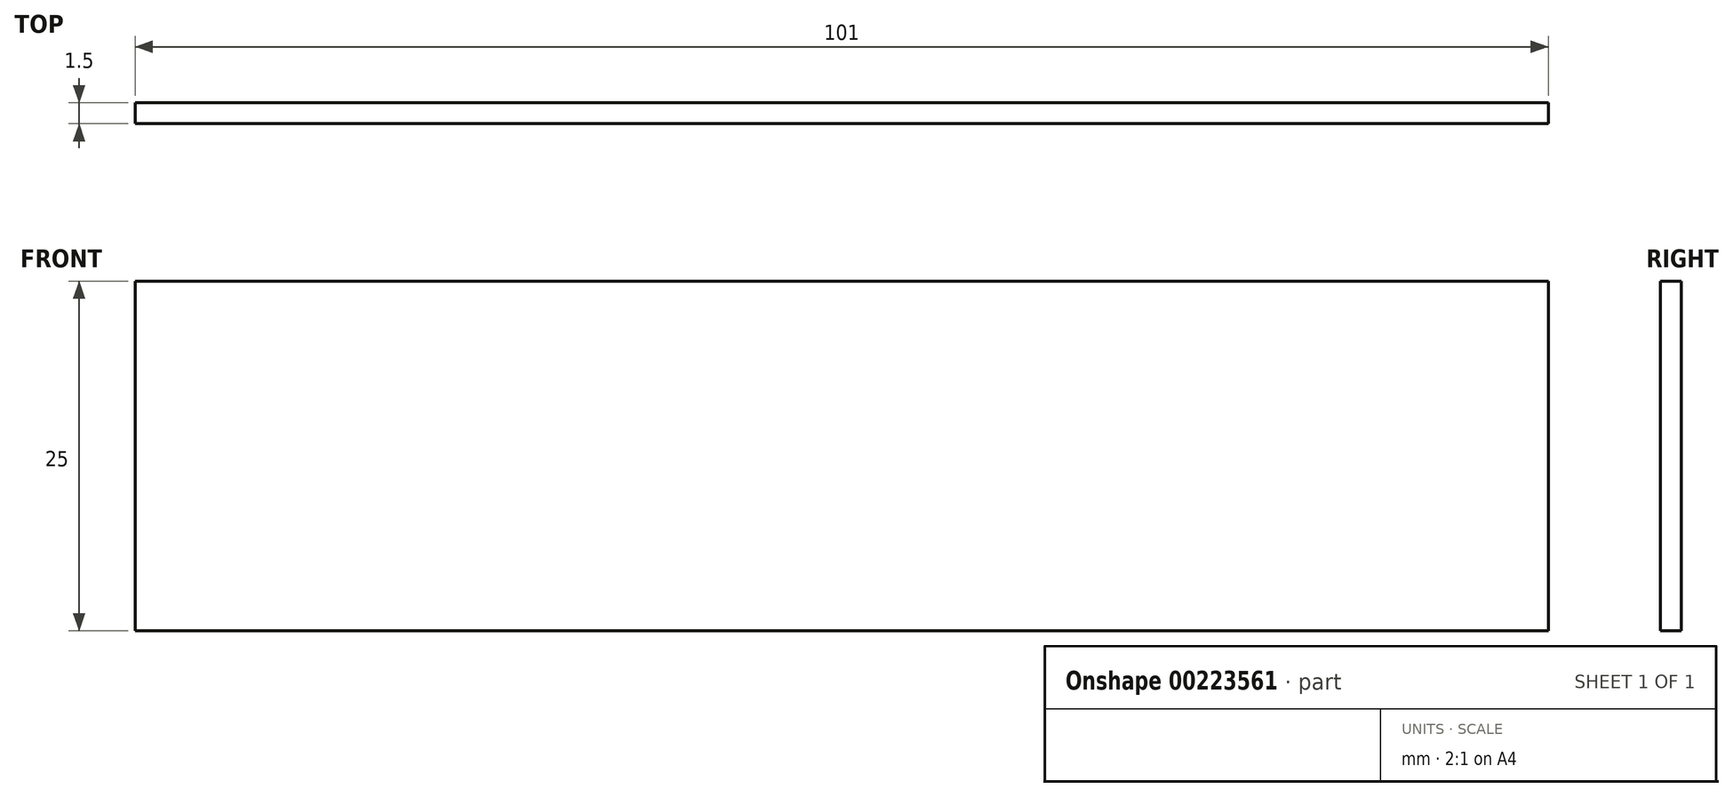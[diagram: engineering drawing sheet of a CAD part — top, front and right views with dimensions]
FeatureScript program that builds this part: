
annotation { "Feature Type Name" : "Feature", "Feature Type Description" : "" }
export const myFeature = defineFeature(function(context is Context, id is Id, definition is map)
    precondition{}
    {
        {
            var Q0;
            Q0=qCreatedBy(makeId("Front.planeOp"),FACE);
            var sketch = newSketch(context, id + "F0", { "sketchPlane" : qUnion([Q0])});
            skLineSegment(sketch, "E0.bottom", {"start": v(50.5, -12.5) * mm, "end": v(-50.5, -12.5) * mm});
            skLineSegment(sketch, "E0.top", {"start": v(50.5, 12.5) * mm, "end": v(-50.5, 12.5) * mm});
            skLineSegment(sketch, "E0.left", {"start": v(50.5, -12.5) * mm, "end": v(50.5, 12.5) * mm});
            skLineSegment(sketch, "E0.right", {"start": v(-50.5, -12.5) * mm, "end": v(-50.5, 12.5) * mm});
            skPoint(sketch, "E0.middle", {"position": v(0, 0) * mm});
            skSolve(sketch);
        }
        {
            var Q0;
            Q0=makeQuery(id+"F0.imprint","IMPRINT",FACE,{"disambiguationData":[TD([[makeQuery(id+"F0.imprint","IMPRINT",EDGE,{"derivedFrom":sQuery(id+"F0.wireOp",EDGE,"E0.bottom")}),-1.0]])]});
            extrude(context, id + "F1", {"entities" : qUnion([Q0]), "depth" : 1.5 * mm});
        }
    });
